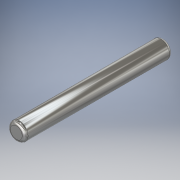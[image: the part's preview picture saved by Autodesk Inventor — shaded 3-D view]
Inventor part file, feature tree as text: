
AUTODESK INVENTOR PART (.ipt)
format: ipt  version: 2018 (Build 220112000, 112)  size: 110,592 bytes
history: native  units: in
note: dims shown in document units (in); Inventor stores cm internally (conversion verified against a paired STEP export)
features: extrude x1, fillet x1, sketch x1
ambient origin geometry x8: Origin, YZ Plane, XZ Plane, XY Plane, X Axis, Y Axis, Z Axis, Center Point
bodies: Solid1 (feature_tree)
feature tree (3):
  extrude  "Extrusion1"  Depth=0.5in TaperAngle=0.0deg
  fillet  "Fillet1"  Radius=0.01in
  sketch  "Sketch1"  dims[d0=0.06in d1=0.5in d2=0.0in d3=0.01in]
